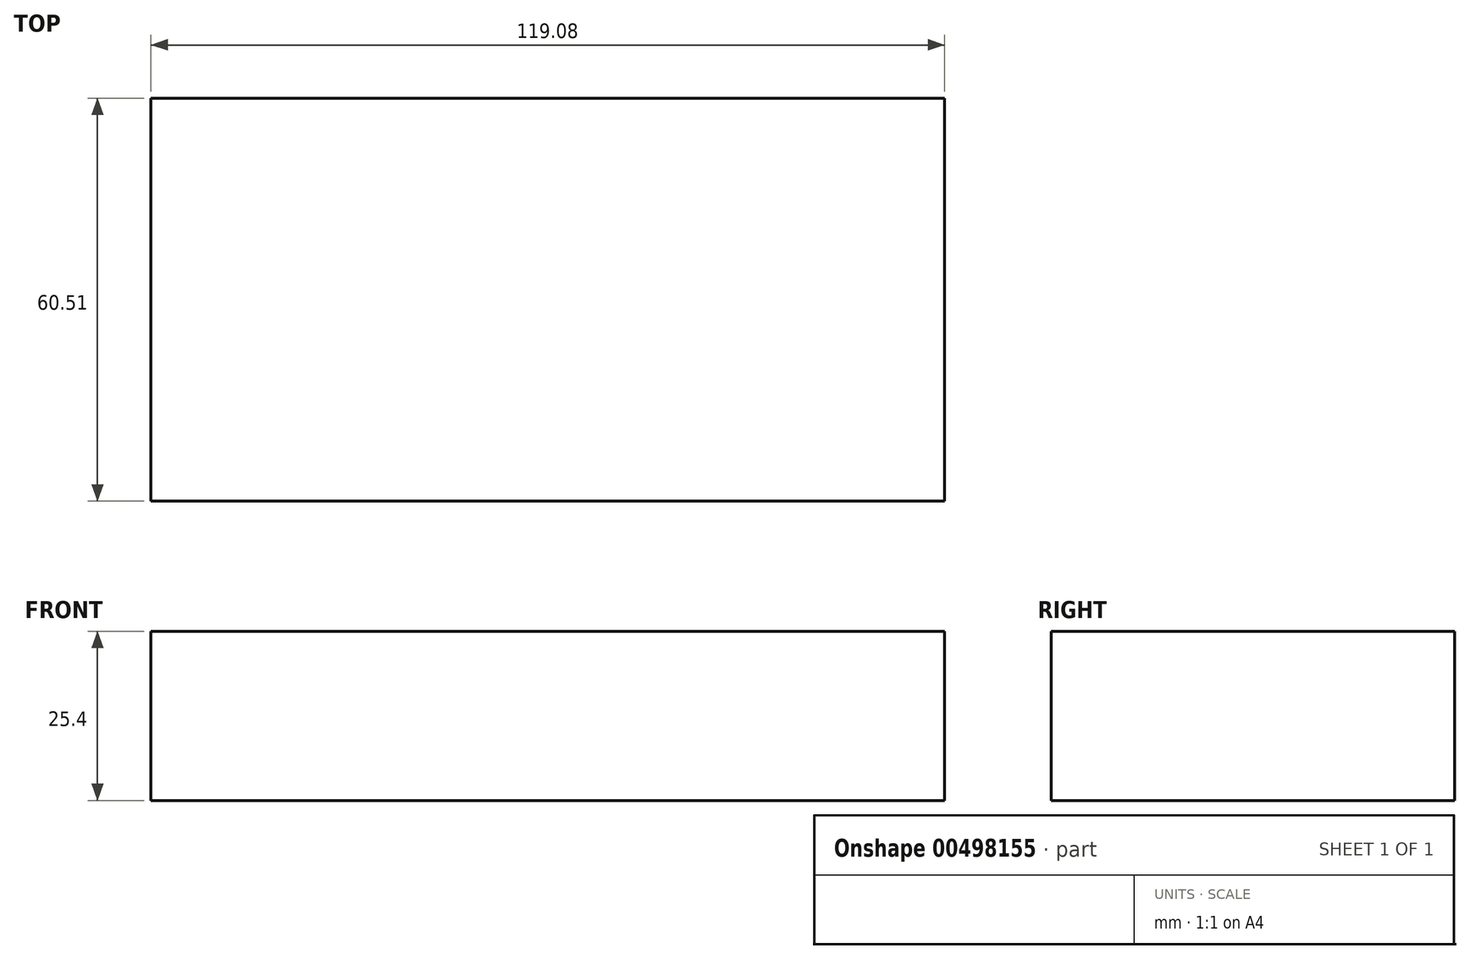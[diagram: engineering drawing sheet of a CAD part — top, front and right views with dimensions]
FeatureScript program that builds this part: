
annotation { "Feature Type Name" : "Feature", "Feature Type Description" : "" }
export const myFeature = defineFeature(function(context is Context, id is Id, definition is map)
    precondition{}
    {
        {
            var Q0;
            Q0=qCreatedBy(makeId("Top.planeOp"),FACE);
            var sketch = newSketch(context, id + "F0", { "sketchPlane" : qUnion([Q0])});
            skLineSegment(sketch, "E0.bottom", {"start": v(26.41, 153.86) * mm, "end": v(145.49, 153.86) * mm});
            skLineSegment(sketch, "E0.top", {"start": v(26.41, 93.35) * mm, "end": v(145.49, 93.35) * mm});
            skLineSegment(sketch, "E0.left", {"start": v(26.41, 153.86) * mm, "end": v(26.41, 93.35) * mm});
            skLineSegment(sketch, "E0.right", {"start": v(145.49, 153.86) * mm, "end": v(145.49, 93.35) * mm});
            skSolve(sketch);
        }
        {
            var Q0;
            Q0=makeQuery(id+"F0.imprint","IMPRINT",FACE,{"disambiguationData":[TD([[makeQuery(id+"F0.imprint","IMPRINT",EDGE,{"derivedFrom":sQuery(id+"F0.wireOp",EDGE,"E0.bottom")}),-1.0]])]});
            extrude(context, id + "F1", {"entities" : qUnion([Q0]), "depth" : 25.4 * mm});
        }
    });
